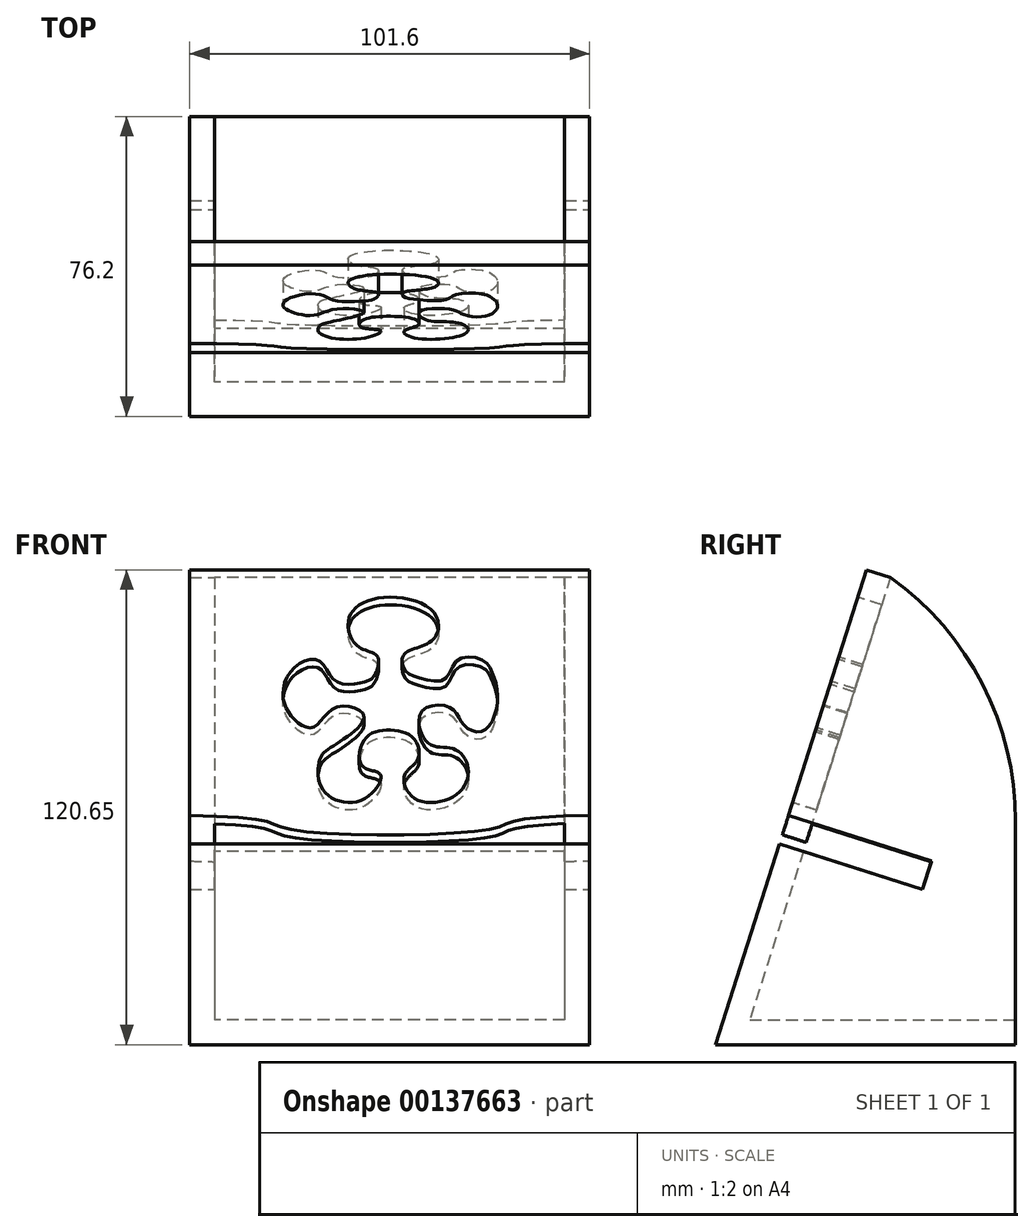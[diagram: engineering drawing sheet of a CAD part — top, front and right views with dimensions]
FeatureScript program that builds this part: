
annotation { "Feature Type Name" : "Feature", "Feature Type Description" : "" }
export const myFeature = defineFeature(function(context is Context, id is Id, definition is map)
    precondition{}
    {
        {
            var Q0;
            Q0=qCreatedBy(makeId("Right.planeOp"),FACE);
            var sketch = newSketch(context, id + "F0", { "sketchPlane" : qUnion([Q0])});
            skLineSegment(sketch, "E0", {"start": v(0, 0) * mm, "end": v(38.36, 120.65) * mm});
            skLineSegment(sketch, "E1", {"start": v(38.36, 120.65) * mm, "end": v(44.41, 118.73) * mm});
            skLineSegment(sketch, "E2", {"start": v(44.41, 118.73) * mm, "end": v(8.68, 6.35) * mm});
            skLineSegment(sketch, "E3", {"start": v(8.68, 6.35) * mm, "end": v(76.2, 6.35) * mm});
            skLineSegment(sketch, "E4", {"start": v(76.2, 6.35) * mm, "end": v(76.2, 0) * mm});
            skLineSegment(sketch, "E5", {"start": v(76.2, 0) * mm, "end": v(0, 0) * mm});
            skSolve(sketch);
        }
        {
            var Q0;
            Q0=makeQuery(id+"F0.imprint","IMPRINT",FACE,{"disambiguationData":[TD([[makeQuery(id+"F0.imprint","IMPRINT",EDGE,{"derivedFrom":sQuery(id+"F0.wireOp",EDGE,"E0")}),-1.0]])]});
            extrude(context, id + "F1", {"entities" : qUnion([Q0]), "depth" : 101.6 * mm, "symmetric" : true});
        }
        {
            var Q0;
            Q0=makeQuery(id+"F1.opExtrude","CAP_FACE",FACE,{"disambiguationData":[OSD([sQuery(id+"F0.wireOp",EDGE,"E0"),sQuery(id+"F0.wireOp",EDGE,"E1"),sQuery(id+"F0.wireOp",EDGE,"E2"),sQuery(id+"F0.wireOp",EDGE,"E3"),sQuery(id+"F0.wireOp",EDGE,"E4"),sQuery(id+"F0.wireOp",EDGE,"E5")])],"isStart":false});
            var sketch = newSketch(context, id + "F2", { "sketchPlane" : qUnion([Q0])});
            skLineSegment(sketch, "E6", {"start": v(44.41, 118.73) * mm, "end": v(76.2, 101.52) * mm});
            skLineSegment(sketch, "E7", {"start": v(76.2, 101.52) * mm, "end": v(76.2, 6.35) * mm});
            skSolve(sketch);
        }
        {
            var Q0;
            Q0 = qSketchRegion(id + "F2", true);
            var Q1;
            Q1=makeQuery(id+"F2.imprint","IMPRINT",FACE,{"disambiguationData":[TD([[makeQuery(id+"F2.imprint","IMPRINT",EDGE,{"derivedFrom":sQuery(id+"F2.wireOp",EDGE,"E6")}),-1.0]])]});
            extrude(context, id + "F3", {"entities" : qUnion([Q0, Q1]), "operationType" : NewBodyOperationType.ADD, "oppositeDirection" : true, "depth" : 6.35 * mm});
        }
        {
            var Q0;
            Q0=makeQuery(id+"F1.opExtrude","SWEPT_BODY",BODY,{"disambiguationData":[OSD([sQuery(id+"F0.wireOp",EDGE,"E0"),sQuery(id+"F0.wireOp",EDGE,"E1"),sQuery(id+"F0.wireOp",EDGE,"E2"),sQuery(id+"F0.wireOp",EDGE,"E3"),sQuery(id+"F0.wireOp",EDGE,"E4"),sQuery(id+"F0.wireOp",EDGE,"E5")])]});
            var Q1;
            Q1=qCreatedBy(makeId("Right.planeOp"),FACE);
            mirror(context, id + "F4", {"operationType" : NewBodyOperationType.ADD, "entities" : qUnion([Q0]), "mirrorPlane" : qUnion([Q1])});
        }
        {
            var Q0;
            Q0=makeQuery(id+"F1.opExtrude","SWEPT_FACE",FACE,{"disambiguationData":[OSD([sQuery(id+"F0.wireOp",EDGE,"E0")])]});
            var sketch = newSketch(context, id + "F5", { "sketchPlane" : qUnion([Q0])});
            skLineSegment(sketch, "E8.top", {"start": v(-115.95, 53.57) * mm, "end": v(111.49, 53.57) * mm});
            skLineSegment(sketch, "E8.left", {"start": v(-115.95, 59.92) * mm, "end": v(-115.95, 53.57) * mm});
            skLineSegment(sketch, "E8.right", {"start": v(111.49, 59.92) * mm, "end": v(111.49, 53.57) * mm});
            skFitSpline(sketch, "E9", {"points": [v(-115.95, 59.92) * mm, v(-33.02, 59.92) * mm, v(-25.4, 57.38) * mm, v(25.4, 57.38) * mm, v(33.02, 59.92) * mm, v(111.49, 59.92) * mm], "startDerivative": vector(219.9, 8.59) * mm, "endDerivative": vector(226.74, -12.42) * mm});
            skSolve(sketch);
        }
        {
            var Q0;
            {var subQ0=sQuery(id+"F5.wireOp",EDGE,"E8.bottom");var subQ1=sQuery(id+"F0.wireOp",EDGE,"E0");var subQ2=makeQuery(id+"F1.opExtrude","CAP_EDGE",EDGE,{"disambiguationData":[OSD([subQ1])],"isStart":true});var subQ3=makeQuery(id+"F5.imprint","INTERSECT",VERTEX,{"derivedFrom":[subQ2,subQ0]});Q0=makeQuery(id+"F5.imprint","IMPRINT",FACE,{"disambiguationData":[TD([[makeQuery(id+"F5.imprint","IMPRINT",EDGE,{"disambiguationData":[TD([[subQ3,-1.0]])],"derivedFrom":subQ0}),-1.0]])]});}
            var Q1;
            {var subQ0=sQuery(id+"F5.wireOp",EDGE,"E8.right");Q1=makeQuery(id+"F5.imprint","IMPRINT",FACE,{"disambiguationData":[TD([[makeQuery(id+"F5.imprint","IMPRINT",EDGE,{"derivedFrom":subQ0}),-1.0]])]});}
            var Q2;
            {var subQ0=sQuery(id+"F5.wireOp",EDGE,"E8.left");Q2=makeQuery(id+"F5.imprint","IMPRINT",FACE,{"disambiguationData":[TD([[makeQuery(id+"F5.imprint","IMPRINT",EDGE,{"derivedFrom":subQ0}),1.0]])]});}
            var Q3;
            {var subQ0=sQuery(id+"F5.wireOp",EDGE,"E8.top");var subQ1=sQuery(id+"F0.wireOp",EDGE,"E0");var subQ2=makeQuery(id+"F1.opExtrude","CAP_EDGE",EDGE,{"disambiguationData":[OSD([subQ1])],"isStart":true});var subQ3=makeQuery(id+"F5.imprint","INTERSECT",VERTEX,{"derivedFrom":[subQ2,subQ0]});Q3=makeQuery(id+"F5.imprint","IMPRINT",FACE,{"disambiguationData":[TD([[makeQuery(id+"F5.imprint","IMPRINT",EDGE,{"disambiguationData":[TD([[subQ3,-1.0]])],"derivedFrom":subQ0}),1.0]])]});}
            extrude(context, id + "F6", {"entities" : qUnion([Q0, Q1, Q2, Q3]), "operationType" : NewBodyOperationType.REMOVE, "oppositeDirection" : true, "depth" : 38.1 * mm});
        }
        {
            var Q0;
            Q0=makeQuery(id+"F3.opExtrude","SWEPT_EDGE",EDGE,{"disambiguationData":[OSD([sQuery(id+"F2.wireOp",EDGE,"E6"),sQuery(id+"F2.wireOp",EDGE,"E7")])]});
            var Q1;
            Q1=makeQuery(id+"F4.opPattern","COPY",EDGE,{"derivedFrom":makeQuery(id+"F3.opExtrude","SWEPT_EDGE",EDGE,{"disambiguationData":[OSD([sQuery(id+"F2.wireOp",EDGE,"E6"),sQuery(id+"F2.wireOp",EDGE,"E7")])]}),"instanceName":"1"});
            fillet(context, id + "F7", {"entities" : qUnion([Q0, Q1]), "radius" : 76.2 * mm, "tangentPropagation" : true, "allowEdgeOverflow" : false});
        }
        {
            var Q0;
            {var subQ0=sQuery(id+"F0.wireOp",EDGE,"E1");var subQ5=sQuery(id+"F0.wireOp",EDGE,"E0");Q0=makeQuery(id+"F6.boolean.opBoolean","SPLIT",FACE,{"disambiguationData":[TD([makeQuery(id+"F1.opExtrude","SWEPT_FACE",FACE,{"disambiguationData":[OSD([subQ0])]})])],"derivedFrom":makeQuery(id+"F1.opExtrude","SWEPT_FACE",FACE,{"disambiguationData":[OSD([subQ5])]})});}
            var sketch = newSketch(context, id + "F8", { "sketchPlane" : qUnion([Q0])});
            skFitSpline(sketch, "E10", {"points": [v(-4.02, 98.3) * mm, v(-3.12, 103.45) * mm, v(-7.28, 105.65) * mm, v(-10.35, 110.07) * mm, v(-9.44, 115.58) * mm, v(-0.95, 119.26) * mm, v(11.34, 115.03) * mm, v(10.7, 107.68) * mm, v(3.77, 104.18) * mm, v(3.77, 99.95) * mm, v(7, 97.93) * mm, v(13.86, 97.38) * mm, v(17.3, 102.53) * mm, v(23.76, 102.42) * mm, v(26.15, 98.85) * mm, v(27.42, 92.6) * mm, v(23.98, 83.77) * mm, v(18.9, 85.1) * mm, v(15.55, 89.74) * mm, v(8.08, 88.74) * mm, v(9.89, 80.28) * mm, v(15.85, 79) * mm, v(19.83, 74.2) * mm, v(17.12, 66.85) * mm, v(6.82, 65.38) * mm, v(3.77, 71.82) * mm, v(7.18, 76.23) * mm, v(5.73, 81.93) * mm, v(-0.66, 83.89) * mm, v(-6.37, 81.38) * mm, v(-6.87, 74.16) * mm, v(-2.4, 72) * mm, v(-7.1, 65.2) * mm, v(-16.85, 67.77) * mm, v(-17.76, 76.05) * mm, v(-14.53, 79.54) * mm, v(-6.55, 87.45) * mm, v(-13.42, 90.02) * mm, v(-19.38, 84.7) * mm, v(-24.26, 86.71) * mm, v(-27.15, 93.15) * mm, v(-24.08, 100.69) * mm, v(-17.94, 102.34) * mm, v(-13.6, 96.83) * mm, v(-6.73, 96.64) * mm, v(-4.02, 98.3) * mm]});
            skSolve(sketch);
        }
        {
            var Q0;
            Q0=makeQuery(id+"F8.imprint","IMPRINT",FACE,{"disambiguationData":[TD([[makeQuery(id+"F8.imprint","IMPRINT",EDGE,{"derivedFrom":sQuery(id+"F8.wireOp",EDGE,"1de80ee6-f3c9-435a-af16-1988c2c9c45f")}),-1.0]])]});
            var Q1;
            Q1=makeQuery(id+"F8.imprint","IMPRINT",FACE,{"disambiguationData":[TD([[makeQuery(id+"F8.imprint","IMPRINT",EDGE,{"derivedFrom":sQuery(id+"F8.wireOp",EDGE,"E10")}),-1.0]])]});
            extrude(context, id + "F9", {"entities" : qUnion([Q0, Q1]), "operationType" : NewBodyOperationType.REMOVE, "oppositeDirection" : true, "depth" : 25.4 * mm});
        }
    });
